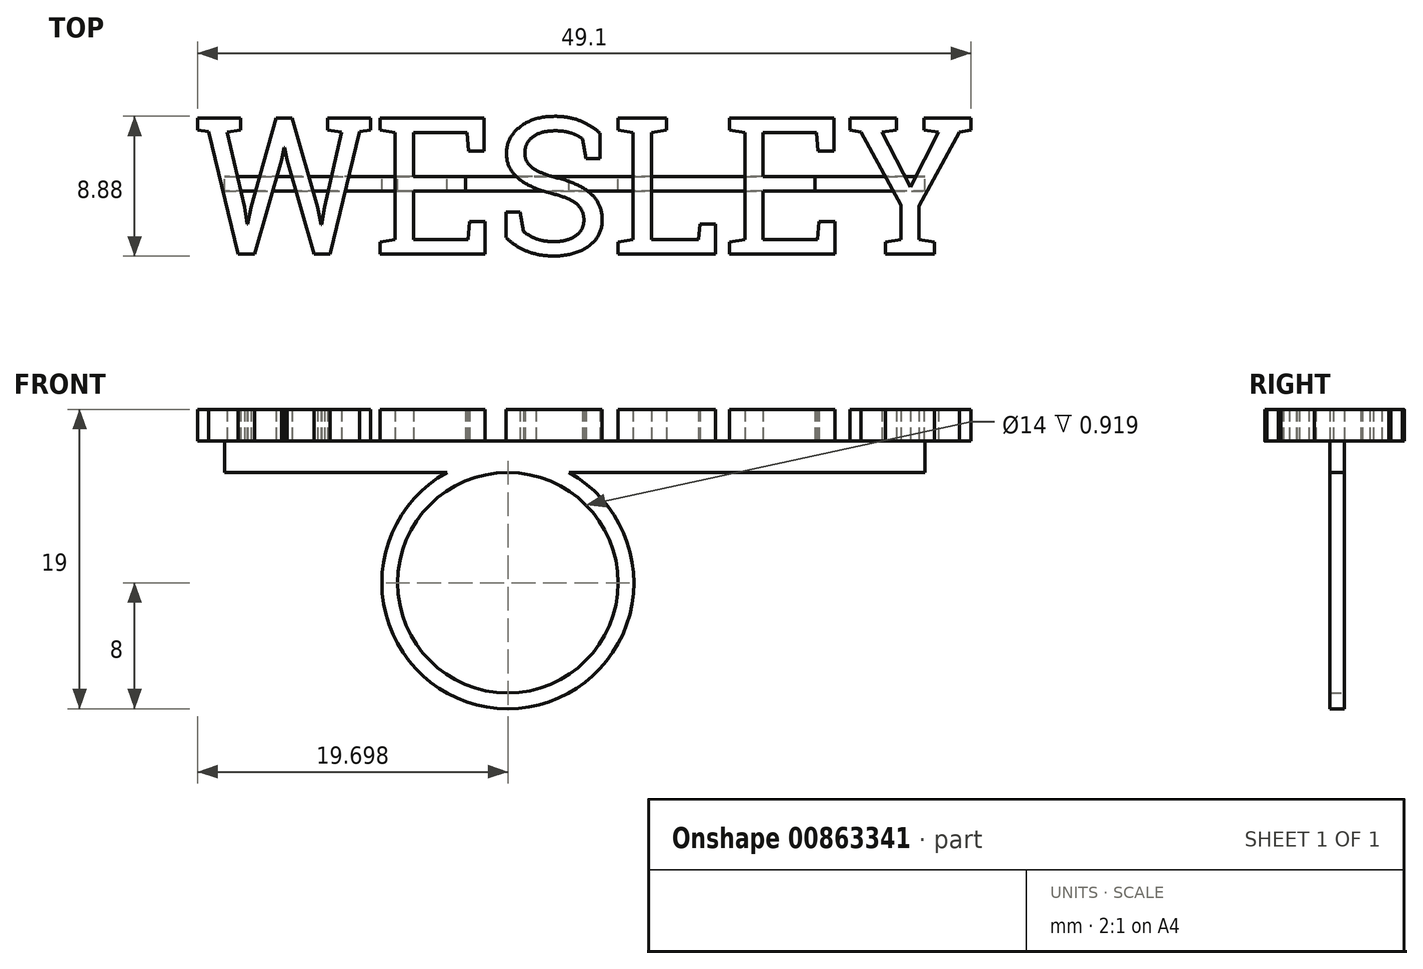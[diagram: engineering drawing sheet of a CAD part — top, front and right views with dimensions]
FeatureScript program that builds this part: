
annotation { "Feature Type Name" : "Feature", "Feature Type Description" : "" }
export const myFeature = defineFeature(function(context is Context, id is Id, definition is map)
    precondition{}
    {
        {
            var Q0;
            Q0=qCreatedBy(makeId("Top.planeOp"),FACE);
            var sketch = newSketch(context, id + "F0", { "sketchPlane" : qUnion([Q0])});
            skText(sketch, "E0", { "text": "WESLEY", "fontName": "RobotoSlab-Regular.ttf"});
            const initialGuessF0  = {"E0": [0, 0, 1, 0, 0.00873]};
            skSetInitialGuess(sketch, initialGuessF0);
            skSolve(sketch);
        }
        {
            var Q0;
            Q0 = qSketchRegion(id + "F0", true);
            extrude(context, id + "F1", {"entities" : qUnion([Q0]), "depth" : 2 * mm, "offsetDistance" : 25 * mm});
        }
        {
            var Q0;
            Q0=makeQuery(id+"F1.opExtrude","CAP_FACE",FACE,{"disambiguationData":[OSD([sQuery(id+"F0.wireOp",EDGE,"E0.sketch_text.stroke-30"),sQuery(id+"F0.wireOp",EDGE,"E0.sketch_text.stroke-31"),sQuery(id+"F0.wireOp",EDGE,"E0.sketch_text.stroke-32"),sQuery(id+"F0.wireOp",EDGE,"E0.sketch_text.stroke-33"),sQuery(id+"F0.wireOp",EDGE,"E0.sketch_text.stroke-34"),sQuery(id+"F0.wireOp",EDGE,"E0.sketch_text.stroke-35"),sQuery(id+"F0.wireOp",EDGE,"E0.sketch_text.stroke-36"),sQuery(id+"F0.wireOp",EDGE,"E0.sketch_text.stroke-37"),sQuery(id+"F0.wireOp",EDGE,"E0.sketch_text.stroke-38"),sQuery(id+"F0.wireOp",EDGE,"E0.sketch_text.stroke-39"),sQuery(id+"F0.wireOp",EDGE,"E0.sketch_text.stroke-40"),sQuery(id+"F0.wireOp",EDGE,"E0.sketch_text.stroke-41"),sQuery(id+"F0.wireOp",EDGE,"E0.sketch_text.stroke-42"),sQuery(id+"F0.wireOp",EDGE,"E0.sketch_text.stroke-43"),sQuery(id+"F0.wireOp",EDGE,"E0.sketch_text.stroke-44"),sQuery(id+"F0.wireOp",EDGE,"E0.sketch_text.stroke-45"),sQuery(id+"F0.wireOp",EDGE,"E0.sketch_text.stroke-46"),sQuery(id+"F0.wireOp",EDGE,"E0.sketch_text.stroke-47"),sQuery(id+"F0.wireOp",EDGE,"E0.sketch_text.stroke-48"),sQuery(id+"F0.wireOp",EDGE,"E0.sketch_text.stroke-49")])],"isStart":true});
            var sketch = newSketch(context, id + "F2", { "sketchPlane" : qUnion([Q0])});
            skLineSegment(sketch, "E1.bottom", {"start": v(13.86, -4) * mm, "end": v(46.36, -4) * mm});
            skLineSegment(sketch, "E1.top", {"start": v(13.86, -4.91) * mm, "end": v(46.36, -4.91) * mm});
            skLineSegment(sketch, "E1.left", {"start": v(13.86, -4) * mm, "end": v(13.86, -4.91) * mm});
            skLineSegment(sketch, "E1.right", {"start": v(46.36, -4) * mm, "end": v(46.36, -4.91) * mm});
            skLineSegment(sketch, "E2.bottom", {"start": v(13.86, -4) * mm, "end": v(1.86, -4) * mm});
            skLineSegment(sketch, "E2.top", {"start": v(13.86, -4.91) * mm, "end": v(1.86, -4.91) * mm});
            skLineSegment(sketch, "E2.right", {"start": v(1.86, -4) * mm, "end": v(1.86, -4.91) * mm});
            skSolve(sketch);
        }
        {
            var Q0;
            Q0 = qSketchRegion(id + "F2", true);
            extrude(context, id + "F3", {"entities" : qUnion([Q0]), "depth" : 2 * mm, "offsetDistance" : 25 * mm});
        }
        {
            var Q0;
            Q0=makeQuery(id+"F1.opExtrude","SWEPT_BODY",BODY,{"disambiguationData":[OSD([sQuery(id+"F0.wireOp",EDGE,"E0.sketch_text.stroke-0"),sQuery(id+"F0.wireOp",EDGE,"E0.sketch_text.stroke-1"),sQuery(id+"F0.wireOp",EDGE,"E0.sketch_text.stroke-2"),sQuery(id+"F0.wireOp",EDGE,"E0.sketch_text.stroke-3"),sQuery(id+"F0.wireOp",EDGE,"E0.sketch_text.stroke-4"),sQuery(id+"F0.wireOp",EDGE,"E0.sketch_text.stroke-5"),sQuery(id+"F0.wireOp",EDGE,"E0.sketch_text.stroke-6"),sQuery(id+"F0.wireOp",EDGE,"E0.sketch_text.stroke-7"),sQuery(id+"F0.wireOp",EDGE,"E0.sketch_text.stroke-8"),sQuery(id+"F0.wireOp",EDGE,"E0.sketch_text.stroke-9"),sQuery(id+"F0.wireOp",EDGE,"E0.sketch_text.stroke-10"),sQuery(id+"F0.wireOp",EDGE,"E0.sketch_text.stroke-11"),sQuery(id+"F0.wireOp",EDGE,"E0.sketch_text.stroke-12"),sQuery(id+"F0.wireOp",EDGE,"E0.sketch_text.stroke-13"),sQuery(id+"F0.wireOp",EDGE,"E0.sketch_text.stroke-14"),sQuery(id+"F0.wireOp",EDGE,"E0.sketch_text.stroke-15"),sQuery(id+"F0.wireOp",EDGE,"E0.sketch_text.stroke-16"),sQuery(id+"F0.wireOp",EDGE,"E0.sketch_text.stroke-17"),sQuery(id+"F0.wireOp",EDGE,"E0.sketch_text.stroke-18"),sQuery(id+"F0.wireOp",EDGE,"E0.sketch_text.stroke-19"),sQuery(id+"F0.wireOp",EDGE,"E0.sketch_text.stroke-20"),sQuery(id+"F0.wireOp",EDGE,"E0.sketch_text.stroke-21"),sQuery(id+"F0.wireOp",EDGE,"E0.sketch_text.stroke-22"),sQuery(id+"F0.wireOp",EDGE,"E0.sketch_text.stroke-23"),sQuery(id+"F0.wireOp",EDGE,"E0.sketch_text.stroke-24"),sQuery(id+"F0.wireOp",EDGE,"E0.sketch_text.stroke-25"),sQuery(id+"F0.wireOp",EDGE,"E0.sketch_text.stroke-26"),sQuery(id+"F0.wireOp",EDGE,"E0.sketch_text.stroke-27"),sQuery(id+"F0.wireOp",EDGE,"E0.sketch_text.stroke-28"),sQuery(id+"F0.wireOp",EDGE,"E0.sketch_text.stroke-29")])]});
            var Q1;
            Q1=makeQuery(id+"F3.opExtrude","SWEPT_BODY",BODY,{"disambiguationData":[OSD([sQuery(id+"F2.wireOp",EDGE,"E1.bottom"),sQuery(id+"F2.wireOp",EDGE,"E1.top"),sQuery(id+"F2.wireOp",EDGE,"E1.right"),sQuery(id+"F2.wireOp",EDGE,"E2.bottom"),sQuery(id+"F2.wireOp",EDGE,"E2.top"),sQuery(id+"F2.wireOp",EDGE,"E2.right")])]});
            var Q2;
            Q2=makeQuery(id+"F1.opExtrude","SWEPT_BODY",BODY,{"disambiguationData":[OSD([sQuery(id+"F0.wireOp",EDGE,"E0.sketch_text.stroke-30"),sQuery(id+"F0.wireOp",EDGE,"E0.sketch_text.stroke-31"),sQuery(id+"F0.wireOp",EDGE,"E0.sketch_text.stroke-32"),sQuery(id+"F0.wireOp",EDGE,"E0.sketch_text.stroke-33"),sQuery(id+"F0.wireOp",EDGE,"E0.sketch_text.stroke-34"),sQuery(id+"F0.wireOp",EDGE,"E0.sketch_text.stroke-35"),sQuery(id+"F0.wireOp",EDGE,"E0.sketch_text.stroke-36"),sQuery(id+"F0.wireOp",EDGE,"E0.sketch_text.stroke-37"),sQuery(id+"F0.wireOp",EDGE,"E0.sketch_text.stroke-38"),sQuery(id+"F0.wireOp",EDGE,"E0.sketch_text.stroke-39"),sQuery(id+"F0.wireOp",EDGE,"E0.sketch_text.stroke-40"),sQuery(id+"F0.wireOp",EDGE,"E0.sketch_text.stroke-41"),sQuery(id+"F0.wireOp",EDGE,"E0.sketch_text.stroke-42"),sQuery(id+"F0.wireOp",EDGE,"E0.sketch_text.stroke-43"),sQuery(id+"F0.wireOp",EDGE,"E0.sketch_text.stroke-44"),sQuery(id+"F0.wireOp",EDGE,"E0.sketch_text.stroke-45"),sQuery(id+"F0.wireOp",EDGE,"E0.sketch_text.stroke-46"),sQuery(id+"F0.wireOp",EDGE,"E0.sketch_text.stroke-47"),sQuery(id+"F0.wireOp",EDGE,"E0.sketch_text.stroke-48"),sQuery(id+"F0.wireOp",EDGE,"E0.sketch_text.stroke-49")])]});
            var Q3;
            Q3=makeQuery(id+"F1.opExtrude","SWEPT_BODY",BODY,{"disambiguationData":[OSD([sQuery(id+"F0.wireOp",EDGE,"E0.sketch_text.stroke-50"),sQuery(id+"F0.wireOp",EDGE,"E0.sketch_text.stroke-51"),sQuery(id+"F0.wireOp",EDGE,"E0.sketch_text.stroke-52"),sQuery(id+"F0.wireOp",EDGE,"E0.sketch_text.stroke-53"),sQuery(id+"F0.wireOp",EDGE,"E0.sketch_text.stroke-54"),sQuery(id+"F0.wireOp",EDGE,"E0.sketch_text.stroke-55"),sQuery(id+"F0.wireOp",EDGE,"E0.sketch_text.stroke-56"),sQuery(id+"F0.wireOp",EDGE,"E0.sketch_text.stroke-57"),sQuery(id+"F0.wireOp",EDGE,"E0.sketch_text.stroke-58"),sQuery(id+"F0.wireOp",EDGE,"E0.sketch_text.stroke-59"),sQuery(id+"F0.wireOp",EDGE,"E0.sketch_text.stroke-60"),sQuery(id+"F0.wireOp",EDGE,"E0.sketch_text.stroke-61"),sQuery(id+"F0.wireOp",EDGE,"E0.sketch_text.stroke-62"),sQuery(id+"F0.wireOp",EDGE,"E0.sketch_text.stroke-63"),sQuery(id+"F0.wireOp",EDGE,"E0.sketch_text.stroke-64"),sQuery(id+"F0.wireOp",EDGE,"E0.sketch_text.stroke-65"),sQuery(id+"F0.wireOp",EDGE,"E0.sketch_text.stroke-66"),sQuery(id+"F0.wireOp",EDGE,"E0.sketch_text.stroke-67"),sQuery(id+"F0.wireOp",EDGE,"E0.sketch_text.stroke-68"),sQuery(id+"F0.wireOp",EDGE,"E0.sketch_text.stroke-69"),sQuery(id+"F0.wireOp",EDGE,"E0.sketch_text.stroke-70"),sQuery(id+"F0.wireOp",EDGE,"E0.sketch_text.stroke-71"),sQuery(id+"F0.wireOp",EDGE,"E0.sketch_text.stroke-72"),sQuery(id+"F0.wireOp",EDGE,"E0.sketch_text.stroke-73"),sQuery(id+"F0.wireOp",EDGE,"E0.sketch_text.stroke-74"),sQuery(id+"F0.wireOp",EDGE,"E0.sketch_text.stroke-75"),sQuery(id+"F0.wireOp",EDGE,"E0.sketch_text.stroke-76"),sQuery(id+"F0.wireOp",EDGE,"E0.sketch_text.stroke-77"),sQuery(id+"F0.wireOp",EDGE,"E0.sketch_text.stroke-78"),sQuery(id+"F0.wireOp",EDGE,"E0.sketch_text.stroke-79")])]});
            var Q4;
            Q4=makeQuery(id+"F1.opExtrude","SWEPT_BODY",BODY,{"disambiguationData":[OSD([sQuery(id+"F0.wireOp",EDGE,"E0.sketch_text.stroke-80"),sQuery(id+"F0.wireOp",EDGE,"E0.sketch_text.stroke-81"),sQuery(id+"F0.wireOp",EDGE,"E0.sketch_text.stroke-82"),sQuery(id+"F0.wireOp",EDGE,"E0.sketch_text.stroke-83"),sQuery(id+"F0.wireOp",EDGE,"E0.sketch_text.stroke-84"),sQuery(id+"F0.wireOp",EDGE,"E0.sketch_text.stroke-85"),sQuery(id+"F0.wireOp",EDGE,"E0.sketch_text.stroke-86"),sQuery(id+"F0.wireOp",EDGE,"E0.sketch_text.stroke-87"),sQuery(id+"F0.wireOp",EDGE,"E0.sketch_text.stroke-88"),sQuery(id+"F0.wireOp",EDGE,"E0.sketch_text.stroke-89"),sQuery(id+"F0.wireOp",EDGE,"E0.sketch_text.stroke-90"),sQuery(id+"F0.wireOp",EDGE,"E0.sketch_text.stroke-91"),sQuery(id+"F0.wireOp",EDGE,"E0.sketch_text.stroke-92"),sQuery(id+"F0.wireOp",EDGE,"E0.sketch_text.stroke-93"),sQuery(id+"F0.wireOp",EDGE,"E0.sketch_text.stroke-94"),sQuery(id+"F0.wireOp",EDGE,"E0.sketch_text.stroke-95")])]});
            var Q5;
            Q5=makeQuery(id+"F1.opExtrude","SWEPT_BODY",BODY,{"disambiguationData":[OSD([sQuery(id+"F0.wireOp",EDGE,"E0.sketch_text.stroke-96"),sQuery(id+"F0.wireOp",EDGE,"E0.sketch_text.stroke-97"),sQuery(id+"F0.wireOp",EDGE,"E0.sketch_text.stroke-98"),sQuery(id+"F0.wireOp",EDGE,"E0.sketch_text.stroke-99"),sQuery(id+"F0.wireOp",EDGE,"E0.sketch_text.stroke-100"),sQuery(id+"F0.wireOp",EDGE,"E0.sketch_text.stroke-101"),sQuery(id+"F0.wireOp",EDGE,"E0.sketch_text.stroke-102"),sQuery(id+"F0.wireOp",EDGE,"E0.sketch_text.stroke-103"),sQuery(id+"F0.wireOp",EDGE,"E0.sketch_text.stroke-104"),sQuery(id+"F0.wireOp",EDGE,"E0.sketch_text.stroke-105"),sQuery(id+"F0.wireOp",EDGE,"E0.sketch_text.stroke-106"),sQuery(id+"F0.wireOp",EDGE,"E0.sketch_text.stroke-107"),sQuery(id+"F0.wireOp",EDGE,"E0.sketch_text.stroke-108"),sQuery(id+"F0.wireOp",EDGE,"E0.sketch_text.stroke-109"),sQuery(id+"F0.wireOp",EDGE,"E0.sketch_text.stroke-110"),sQuery(id+"F0.wireOp",EDGE,"E0.sketch_text.stroke-111"),sQuery(id+"F0.wireOp",EDGE,"E0.sketch_text.stroke-112"),sQuery(id+"F0.wireOp",EDGE,"E0.sketch_text.stroke-113"),sQuery(id+"F0.wireOp",EDGE,"E0.sketch_text.stroke-114"),sQuery(id+"F0.wireOp",EDGE,"E0.sketch_text.stroke-115")])]});
            var Q6;
            Q6=makeQuery(id+"F1.opExtrude","SWEPT_BODY",BODY,{"disambiguationData":[OSD([sQuery(id+"F0.wireOp",EDGE,"E0.sketch_text.stroke-116"),sQuery(id+"F0.wireOp",EDGE,"E0.sketch_text.stroke-117"),sQuery(id+"F0.wireOp",EDGE,"E0.sketch_text.stroke-118"),sQuery(id+"F0.wireOp",EDGE,"E0.sketch_text.stroke-119"),sQuery(id+"F0.wireOp",EDGE,"E0.sketch_text.stroke-120"),sQuery(id+"F0.wireOp",EDGE,"E0.sketch_text.stroke-121"),sQuery(id+"F0.wireOp",EDGE,"E0.sketch_text.stroke-122"),sQuery(id+"F0.wireOp",EDGE,"E0.sketch_text.stroke-123"),sQuery(id+"F0.wireOp",EDGE,"E0.sketch_text.stroke-124"),sQuery(id+"F0.wireOp",EDGE,"E0.sketch_text.stroke-125"),sQuery(id+"F0.wireOp",EDGE,"E0.sketch_text.stroke-126"),sQuery(id+"F0.wireOp",EDGE,"E0.sketch_text.stroke-127"),sQuery(id+"F0.wireOp",EDGE,"E0.sketch_text.stroke-128"),sQuery(id+"F0.wireOp",EDGE,"E0.sketch_text.stroke-129"),sQuery(id+"F0.wireOp",EDGE,"E0.sketch_text.stroke-130"),sQuery(id+"F0.wireOp",EDGE,"E0.sketch_text.stroke-131"),sQuery(id+"F0.wireOp",EDGE,"E0.sketch_text.stroke-132"),sQuery(id+"F0.wireOp",EDGE,"E0.sketch_text.stroke-133"),sQuery(id+"F0.wireOp",EDGE,"E0.sketch_text.stroke-134"),sQuery(id+"F0.wireOp",EDGE,"E0.sketch_text.stroke-135"),sQuery(id+"F0.wireOp",EDGE,"E0.sketch_text.stroke-136")])]});
            booleanBodies(context, id + "F4", {"operationType" : BooleanOperationType.UNION, "tools" : qUnion([Q0, Q1, Q2, Q3, Q4, Q5, Q6])});
        }
        {
            var Q0;
            Q0=makeQuery(id+"F4.opBoolean","MERGE",FACE,{"derivedFrom":[makeQuery(id+"F1.opExtrude","SWEPT_FACE",FACE,{"disambiguationData":[OSD([sQuery(id+"F0.wireOp",EDGE,"E0.sketch_text.stroke-41")])]}),makeQuery(id+"F1.opExtrude","SWEPT_FACE",FACE,{"disambiguationData":[OSD([sQuery(id+"F0.wireOp",EDGE,"E0.sketch_text.stroke-107")])]}),makeQuery(id+"F3.opExtrude","SWEPT_FACE",FACE,{"disambiguationData":[OSD([sQuery(id+"F2.wireOp",EDGE,"E1.top"),sQuery(id+"F2.wireOp",EDGE,"E2.top")])]})]});
            var sketch = newSketch(context, id + "F5", { "sketchPlane" : qUnion([Q0])});
            skCircle(sketch, "E3", {"center": v(-19.86, -9) * mm, "radius": 7 * mm});
            skLineSegment(sketch, "E4", {"start": v(-1.86, -2) * mm, "end": v(-19.86, -2) * mm, "construction": true});
            skCircle(sketch, "E5", {"center": v(-19.86, -9) * mm, "radius": 8 * mm});
            skSolve(sketch);
        }
        {
            var Q0;
            {var subQ0=sQuery(id+"F5.wireOp",EDGE,"E3");Q0=makeQuery(id+"F5.imprint","IMPRINT",FACE,{"disambiguationData":[TD([[makeQuery(id+"F5.imprint","IMPRINT",EDGE,{"derivedFrom":subQ0}),-1.0]])]});}
            var Q1;
            {var subQ0=sQuery(id+"F5.wireOp",EDGE,"E5");var subQ1=makeQuery(id+"F3.opExtrude","CAP_EDGE",EDGE,{"disambiguationData":[OSD([sQuery(id+"F2.wireOp",EDGE,"E1.top"),sQuery(id+"F2.wireOp",EDGE,"E2.top")])],"isStart":false});var subQ2=makeQuery(id+"F5.imprint","INTERSECT",VERTEX,{"disambiguationData":[OD(0.0)],"derivedFrom":[subQ1,subQ0]});Q1=makeQuery(id+"F5.imprint","IMPRINT",FACE,{"disambiguationData":[TD([[makeQuery(id+"F5.imprint","IMPRINT",EDGE,{"disambiguationData":[TD([[subQ2,1.0]])],"derivedFrom":subQ0}),1.0]])]});}
            var Q2;
            Q2=makeQuery(id+"F4.opBoolean","MERGE",FACE,{"derivedFrom":[makeQuery(id+"F1.opExtrude","SWEPT_FACE",FACE,{"disambiguationData":[OSD([sQuery(id+"F0.wireOp",EDGE,"E0.sketch_text.stroke-43")])]}),makeQuery(id+"F1.opExtrude","SWEPT_FACE",FACE,{"disambiguationData":[OSD([sQuery(id+"F0.wireOp",EDGE,"E0.sketch_text.stroke-109")])]}),makeQuery(id+"F3.opExtrude","SWEPT_FACE",FACE,{"disambiguationData":[OSD([sQuery(id+"F2.wireOp",EDGE,"E1.bottom"),sQuery(id+"F2.wireOp",EDGE,"E2.bottom")])]})]});
            extrude(context, id + "F6", {"entities" : qUnion([Q0, Q1]), "operationType" : NewBodyOperationType.ADD, "endBound" : BoundingType.UP_TO_SURFACE, "oppositeDirection" : true, "depth" : 25 * mm, "endBoundEntityFace" : qUnion([Q2]), "offsetDistance" : 25 * mm});
        }
    });
